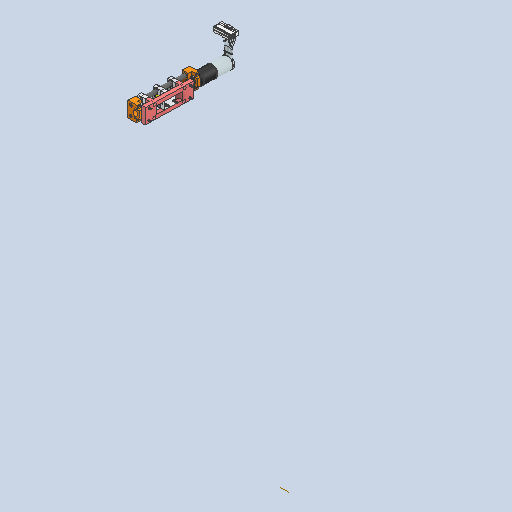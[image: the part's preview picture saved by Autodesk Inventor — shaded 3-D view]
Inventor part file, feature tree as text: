
AUTODESK INVENTOR PART (.ipt)
format: ipt  version: 2023 (Build 270158000, 158)  size: 17,326,080 bytes
history: native  units: mm
features: other x42, sketch x1
ambient origin geometry x8: Origin, YZ Plane, XZ Plane, XY Plane, X Axis, Y Axis, Z Axis, Center Point
bodies: Solid1 (feature_tree), Solid2 (feature_tree), Solid3 (feature_tree), Solid4 (feature_tree), Solid5 (feature_tree), Solid6 (feature_tree), Solid7 (feature_tree), Solid8 (feature_tree), Solid9 (feature_tree), Solid10 (feature_tree), Solid11 (feature_tree), Solid12 (feature_tree), Solid13 (feature_tree), Solid14 (feature_tree), Solid15 (feature_tree), Solid16 (feature_tree), Solid17 (feature_tree), Solid18 (feature_tree), Solid19 (feature_tree), Solid20 (feature_tree), Solid21 (feature_tree), Solid22 (feature_tree), Solid23 (feature_tree), Solid24 (feature_tree), Solid25 (feature_tree), Solid26 (feature_tree), Solid27 (feature_tree), Solid28 (feature_tree), Solid29 (feature_tree), Solid30 (feature_tree), Solid31 (feature_tree), Solid32 (feature_tree), Solid33 (feature_tree), Solid34 (feature_tree), Solid35 (feature_tree), Solid36 (feature_tree), Solid37 (feature_tree), Solid38 (feature_tree), Solid39 (feature_tree), Solid40 (feature_tree)
feature tree (43):
  other  "DifferentialLinearActuator.iam"
  other  "Part1.ipt:1"
  other  "GP16A_2-Stufig-110322.ipt:2"
  other  "283825_ec-max16_5w.ipt:2"
  other  "4145N198_Set Screw Precision Flexible Shaft Couplings.ipt:2"
  other  "91292A832_18-8 Stainless Steel Socket Head Screw.ipt:5"
  other  "91292A832_18-8 Stainless Steel Socket Head Screw.ipt:6"
  other  "MotorMountDifferential.ipt:1"
  other  "93805A627_18-8 Stainless Steel Threaded Rod.ipt:1"
  other  "93805A631_18-8 Stainless Steel Threaded Rod.ipt:2"
  other  "91828A113_18-8 Stainless Steel Hex Nut.ipt:1"
  other  "94450A564_Left-Hand Threaded 18-8 Stainless Steel Thin Hex Nut.ipt:3"
  other  "MotorDifferentialMountingBracket.ipt:1"
  other  "POMSliderMotorM25.ipt:1"
  other  "SliderFixtureM25.ipt:1"
  other  "POMSliderMotor.ipt:3"
  other  "POMSliderMotor.ipt:4"
  other  "91292A832_18-8 Stainless Steel Socket Head Screw.ipt:9"
  other  "91292A832_18-8 Stainless Steel Socket Head Screw.ipt:10"
  other  "91292A832_18-8 Stainless Steel Socket Head Screw.ipt:11"
  other  "91292A832_18-8 Stainless Steel Socket Head Screw.ipt:12"
  other  "91292A832_18-8 Stainless Steel Socket Head Screw.ipt:13"
  other  "91292A832_18-8 Stainless Steel Socket Head Screw.ipt:14"
  other  "91292A832_18-8 Stainless Steel Socket Head Screw.ipt:15"
  other  "91292A832_18-8 Stainless Steel Socket Head Screw.ipt:16"
  other  "91292A832_18-8 Stainless Steel Socket Head Screw.ipt:17"
  other  "91292A832_18-8 Stainless Steel Socket Head Screw.ipt:18"
  other  "AxisJoinerThreaded.ipt:2"
  other  "AxisLinear.ipt:1"
  other  "AxisLinear.ipt:2"
  other  "91292A832_18-8 Stainless Steel Socket Head Screw.ipt:19"
  other  "91292A832_18-8 Stainless Steel Socket Head Screw.ipt:20"
  other  "MotorMountDifferential.ipt:2"
  other  "91292A832_18-8 Stainless Steel Socket Head Screw.ipt:21"
  other  "91292A832_18-8 Stainless Steel Socket Head Screw.ipt:22"
  other  "POMSliderAxis.ipt:1"
  other  "POMSliderAxis.ipt:2"
  other  "POMSliderAxis.ipt:3"
  other  "91292A832_18-8 Stainless Steel Socket Head Screw.ipt:23"
  other  "91292A832_18-8 Stainless Steel Socket Head Screw.ipt:24"
  other  "91292A832_18-8 Stainless Steel Socket Head Screw.ipt:25"
  other  "Work Axis1"
  sketch  "Sketch6"  dims[d0=10.0mm]
